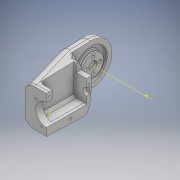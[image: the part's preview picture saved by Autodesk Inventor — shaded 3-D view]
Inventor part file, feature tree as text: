
AUTODESK INVENTOR PART (.ipt)
format: ipt  version: 2018 (Build 220112000, 112)  size: 970,752 bytes
history: native  units: mm
features: projected_geometry x48, sketch x45, extrude x37, hole x13, other x10, chamfer x9, fillet x7, reference x3, mirror x1, plane x1
ambient origin geometry x8: Origin, YZ Plane, XZ Plane, XY Plane, X Axis, Y Axis, Z Axis, Center Point
bodies: Solid1 (feature_tree)
feature tree (174):
  extrude  "Extrusion1"  Depth=45.0mm
  extrude  "Extrusion2"  Depth=2.25mm
  hole  "Hole1"  [1 undecoded]
  hole  "Hole2"  [1 undecoded]
  fillet  "Fillet1"  Radius=14.0mm
  extrude  "Extrusion3"  Depth=18.5mm
  extrude  "Extrusion4"  Depth=10.0mm
  extrude  "Extrusion5"  Depth=2.0mm
  extrude  "Extrusion6"  Depth=8.0mm
  hole  "Hole3"  [1 undecoded]
  extrude  "Extrusion7"  Depth=0.5mm
  extrude  "Extrusion8"  Depth=1.0mm TaperAngle=0.0deg
  extrude  "Extrusion9"  Depth=24.5mm
  extrude  "Extrusion10"  Depth=10.0mm
  extrude  "Extrusion11"  Depth=14.5mm
  extrude  "Extrusion13"  Depth=20.0mm
  extrude  "Extrusion14"  Depth=5.0mm
  extrude  "Extrusion15"  Depth=2.25mm
  extrude  "Extrusion16"  Depth=5.0mm
  extrude  "Extrusion17"  Depth=9.0mm
  chamfer  "Chamfer1"  Distance=1.0mm
  fillet  "Fillet7"  Radius=20.7mm
  fillet  "Fillet8"  Radius=32.0mm
  mirror  "Mirror1"
  sketch  "Sketch26"  dims[d55=2.25mm d56=5.0mm]
  extrude  "Extrusion24"  Depth=1.0mm TaperAngle=0.0deg
  extrude  "Extrusion25"  Depth=8.0mm
  extrude  "Extrusion26"  Depth=0.2mm TaperAngle=0.0deg
  extrude  "Extrusion27"  Depth=8.0mm TaperAngle=0.0deg
  other  "Work Axis1"
  plane  "Work Plane2"
  extrude  "Extrusion28"  Depth=0.2mm TaperAngle=0.0deg
  extrude  "Extrusion29"  Depth=2.5mm TaperAngle=45.0deg
  chamfer  "Chamfer2"  Distance=15.0mm
  extrude  "Extrusion31"  Depth=15.0mm TaperAngle=0.0deg
  chamfer  "Chamfer3"  Distance=15.0mm
  chamfer  "Chamfer4"  Distance=100.0mm
  extrude  "Extrusion32"  Depth=2.0mm TaperAngle=45.0deg
  chamfer  "Chamfer5"  [1 undecoded]
  extrude  "Extrusion33"  Depth=11.5mm
  sketch  "Sketch41"  dims[d100=0.2mm d101=0.0mm d102=2.5mm d103=2.0mm d104=45.0deg]
  extrude  "Extrusion34"  Depth=11.5mm
  chamfer  "Chamfer6"  Distance=11.5mm
  fillet  "Fillet9"  Radius=100.0mm
  extrude  "Extrusion35"  Depth=2.0mm TaperAngle=45.0deg
  extrude  "Extrusion36"  Depth=2.0mm TaperAngle=45.0deg
  chamfer  "Chamfer7"  Distance=7.0mm
  fillet  "Fillet10"  Radius=100.0mm
  extrude  "Extrusion37"  Depth=2.0mm TaperAngle=45.0deg
  extrude  "Extrusion38"  Depth=32.25mm TaperAngle=0.0deg
  extrude  "Extrusion39"  Depth=32.25mm TaperAngle=0.0deg
  extrude  "Extrusion40"  Depth=2.0mm TaperAngle=45.0deg
  chamfer  "Chamfer8"  Distance=8.0mm
  chamfer  "Chamfer9"  Angle=15.0deg  [1 undecoded]
  hole  "Hole6"  [1 undecoded]
  fillet  "Fillet11"  Radius=15.470628mm
  fillet  "Fillet12"  Radius=2.5mm
  extrude  "Extrusion41"  Depth=2.5mm TaperAngle=0.0deg
  extrude  "Extrusion42"  Depth=2.0mm TaperAngle=45.0deg
  hole  "Hole7"  [1 undecoded]
  extrude  "Extrusion43"  TaperAngle=15.0deg  [1 undecoded]
  extrude  "Extrusion44"  Depth=4.0mm
  sketch  "Sketch58"  dims[d162=5.0mm d165=100.0mm d166=0.0mm]
  hole  "Hole8"  [1 undecoded]
  hole  "Hole9"  [1 undecoded]
  hole  "Hole10"  [1 undecoded]
  hole  "Hole11"  [1 undecoded]
  hole  "Hole12"  [1 undecoded]
  hole  "Hole13"  [1 undecoded]
  hole  "Hole14"  [1 undecoded]
  hole  "Hole15"  [1 undecoded]
  extrude  "Extrusion45"  Depth=2.0mm
  sketch  "Sketch1"  dims[d0=24.5mm d1=45.0mm]
  sketch  "Sketch2"  dims[d2=1.95mm d3=0.0mm d4=2.25mm]
  projected_geometry  "Projected Loop1"
  sketch  "Sketch3"  dims[d5=20.0mm d6=2.25mm]
  projected_geometry  "Projected Loop2"
  sketch  "Sketch4"  dims[d7=5.25mm d8=5.25mm d9=14.0mm]
  projected_geometry  "Projected Loop3"
  sketch  "Sketch5"  dims[d10=5.25mm d11=18.5mm]
  projected_geometry  "Projected Loop4"
  sketch  "Sketch6"  dims[d12=10.0mm d13=0.0mm d14=20.5mm]
  projected_geometry  "Projected Loop5"
  sketch  "Sketch7"  dims[d15=2.0mm d16=2.195mm]
  projected_geometry  "Projected Loop6"
  sketch  "Sketch8"  dims[d17=2.0mm]
  projected_geometry  "Projected Loop7"
  sketch  "Sketch9"  dims[d18=2.4mm d19=6.0mm d20=4.4mm d21=2.0mm d22=90.0deg d23=8.0mm d24=20.594885mm d25=20.5mm]
  projected_geometry  "Projected Loop8"
  projected_geometry  "Projected Loop9"
  sketch  "Sketch10"  dims[d26=26.65mm d27=2.0mm]
  projected_geometry  "Projected Loop10"
  projected_geometry  "Projected Loop11"
  sketch  "Sketch11"  dims[d28=2.0mm]
  projected_geometry  "Projected Loop12"
  sketch  "Sketch12"  dims[d29=2.4mm d30=6.0mm d31=4.4mm d32=2.0mm d33=90.0deg d34=8.0mm d35=20.594885mm d36=0.5mm]
  sketch  "Sketch13"  dims[d37=18.0mm d38=1.0mm d39=0.0mm]
  sketch  "Sketch14"  dims[d41=5.0mm d42=0.0mm d43=24.5mm]
  projected_geometry  "Projected Loop13"
  sketch  "Sketch16"  dims[d44=1.15mm d45=0.0mm d46=10.0mm]
  projected_geometry  "Projected Loop14"
  sketch  "Sketch17"  dims[d47=21.0mm d48=14.5mm]
  projected_geometry  "Projected Loop15"
  sketch  "Sketch18"  dims[d49=20.0mm d50=14.5mm]
  projected_geometry  "Projected Loop16"
  sketch  "Sketch19"  dims[d51=24.5mm d52=5.0mm]
  projected_geometry  "Projected Loop17"
  sketch  "Sketch20"  dims[d53=5.0mm d54=2.25mm]
  projected_geometry  "Projected Loop18"
  projected_geometry  "Projected Loop25"
  sketch  "Sketch31"  dims[d57=5.0mm d58=9.0mm]
  projected_geometry  "Projected Loop30"
  reference  "Reference1"
  sketch  "Sketch32"  dims[d59=14.75mm]
  projected_geometry  "Projected Loop31"
  sketch  "Sketch33"  dims[d60=4.0mm d61=1.0mm d62=0.0mm d63=20.7mm]
  projected_geometry  "Projected Loop32"
  sketch  "Sketch34"  dims[d64=2.4mm d65=6.0mm d66=4.4mm d67=2.0mm d68=90.0deg d69=8.0mm d70=20.594885mm d72=32.0mm]
  projected_geometry  "Projected Loop33"
  other  "Work Point1"
  other  "Work Point2"
  other  "Work Point3"
  sketch  "Sketch35"  dims[d73=3.0mm d74=0.0mm d75=1.0mm d76=0.0mm]
  sketch  "Sketch37"  dims[d77=12.25mm d78=0.0mm d80=8.0mm]
  projected_geometry  "Projected Loop34"
  sketch  "Sketch38"  dims[d81=4.5mm d82=0.0mm d84=0.2mm d85=0.0mm]
  sketch  "Sketch39"  dims[d91=8.0mm d92=0.0mm d93=5.0mm d94=0.0mm]
  sketch  "Sketch40"  dims[d95=5.0mm d96=0.0mm d98=0.2mm d99=0.0mm]
  projected_geometry  "Projected Loop35"
  projected_geometry  "Projected Loop36"
  projected_geometry  "Projected Loop37"
  projected_geometry  "Projected Loop38"
  sketch  "Sketch42"  dims[d105=1.5mm]
  projected_geometry  "Projected Loop39"
  sketch  "Sketch43"  dims[d114=0.5mm]
  reference  "Reference2"
  reference  "Reference3"
  sketch  "Sketch45"  dims[d130=60.0mm]
  projected_geometry  "Projected Loop40"
  sketch  "Sketch46"  dims[d131=36.0mm]
  projected_geometry  "Projected Loop41"
  sketch  "Sketch48"  dims[d146=40.0mm]
  projected_geometry  "Projected Loop43"
  sketch  "Sketch49"  dims[d147=60.0mm]
  projected_geometry  "Projected Loop44"
  projected_geometry  "Projected Loop45"
  sketch  "Sketch50"  dims[d148=0.0mm]
  projected_geometry  "Projected Loop46"
  sketch  "Sketch52"  dims[d149=2.3mm d150=15.0mm d151=0.0mm]
  sketch  "Sketch53"  dims[d152=15.0mm d153=0.0mm d154=15.0mm d155=0.0mm d156=15.0mm d157=0.0mm]
  projected_geometry  "Projected Loop47"
  sketch  "Sketch54"  dims[d158=20.5mm]
  projected_geometry  "Projected Loop48"
  sketch  "Sketch55"  dims[d159=41.5mm]
  sketch  "Sketch56"  dims[d160=15.5mm]
  projected_geometry  "Projected Loop49"
  sketch  "Sketch57"  dims[d161=15.5mm]
  projected_geometry  "Projected Loop50"
  projected_geometry  "Projected Loop51"
  projected_geometry  "Projected Loop52"
  projected_geometry  "Projected Loop53"
  projected_geometry  "Projected Loop54"
  projected_geometry  "Projected Loop55"
  projected_geometry  "Projected Loop56"
  projected_geometry  "Projected Loop57"
  sketch  "Sketch59"  dims[d167=100.0mm d168=0.0mm d169=6.0mm d170=2.0mm d171=45.0deg d172=0.0mm d173=11.5mm d175=11.5mm d176=11.5mm d179=100.0mm d180=0.0mm d181=5.0mm d182=2.0mm d183=45.0deg d184=5.0mm d185=2.0mm d186=45.0deg d187=7.0mm d188=100.0mm d189=0.0mm d190=5.0mm d191=2.0mm d192=45.0deg d193=100.0mm d194=0.0mm d195=100.0mm d196=0.0mm d197=5.0mm d198=2.0mm d199=45.0deg d200=8.0mm d202=15.0deg d204=10.970628mm d205=15.470628mm d206=2.5mm d207=0.0mm d208=2.5mm d209=0.0mm d210=3.0mm d211=2.0mm d212=45.0deg d213=2.0mm d215=15.0deg d216=4.0mm d217=4.0mm d218=5.0mm d219=0.0mm d222=32.0mm d223=4.0mm d224=0.0mm d225=2.5mm d226=0.0mm d227=6.5mm d228=0.0mm d229=3.0mm d230=2.0mm d231=45.0deg d232=3.0mm d233=2.0mm d234=45.0deg d235=1.567mm d236=15.0mm d237=4.0mm d238=2.0mm d239=90.0deg d240=15.0mm d241=20.594885mm d242=2.0mm d243=0.75mm d244=20.5mm d245=3.05mm d246=0.0mm d247=14.0mm d248=3.2mm d249=6.0mm d250=4.0mm d251=2.0mm d252=90.0deg d253=8.8mm d254=20.594885mm d255=20.5mm d256=1.55mm d257=0.0mm d258=8.0mm d259=2.5mm d260=0.0mm d261=8.0mm d262=2.5mm d263=0.0mm d266=4.624622mm d267=4.624622mm d268=2.75mm d269=2.75mm d270=2.35mm d271=2.35mm d272=14.0mm d273=4.0mm d274=5.6mm d275=3.708mm d276=3.023mm d277=2.0mm d278=14.3117mm d279=17.0mm d280=0.0mm d281=4.0mm d282=3.708mm d283=3.023mm d284=2.0mm d285=14.3117mm d286=19.0mm d287=0.0mm d288=4.0mm d289=3.708mm d290=3.023mm d291=2.0mm d292=14.3117mm d293=13.0mm d294=0.0mm d295=2.3mm d296=4.0mm d297=4.4mm d298=2.0mm d299=90.0deg d300=32.25mm d301=0.0mm d302=3.3mm d303=4.0mm d304=6.3mm d305=2.0mm d306=90.0deg d307=32.25mm d308=0.0mm d309=1.567mm d310=4.0mm d311=6.3mm d312=2.0mm d313=90.0deg d314=45.0mm d315=20.594885mm d316=1.567mm d317=4.0mm d318=6.3mm d319=2.0mm d320=90.0deg d321=55.0mm d322=20.594885mm d323=2.459mm d324=6.0mm d325=6.3mm d326=2.0mm d327=90.0deg d328=50.0mm d329=20.594885mm d330=32.25mm d331=0.0mm]
  parser-record x1  (decoder bookkeeping rows leaked as tree rows — omitted from the tree; the rows remain in map.json)
  other  "servocheck.iam"
  other  "LX-16A:3"
  other  "DUOPAN-SG-SJ_10"
  projected_geometry  "Project Cut Edges1"
  projected_geometry  "Project Cut Edges3"
  other  "bottomarm:1"
  other  "arm1:1"
note: 16 required parameter values undecoded (feature->parameter linkage not recoverable at this tier; creation-order binding heuristic only, values carry confidence <= 0.55)
note: 1 file-system path scrubbed to <path> (originals preserved in map.json)
